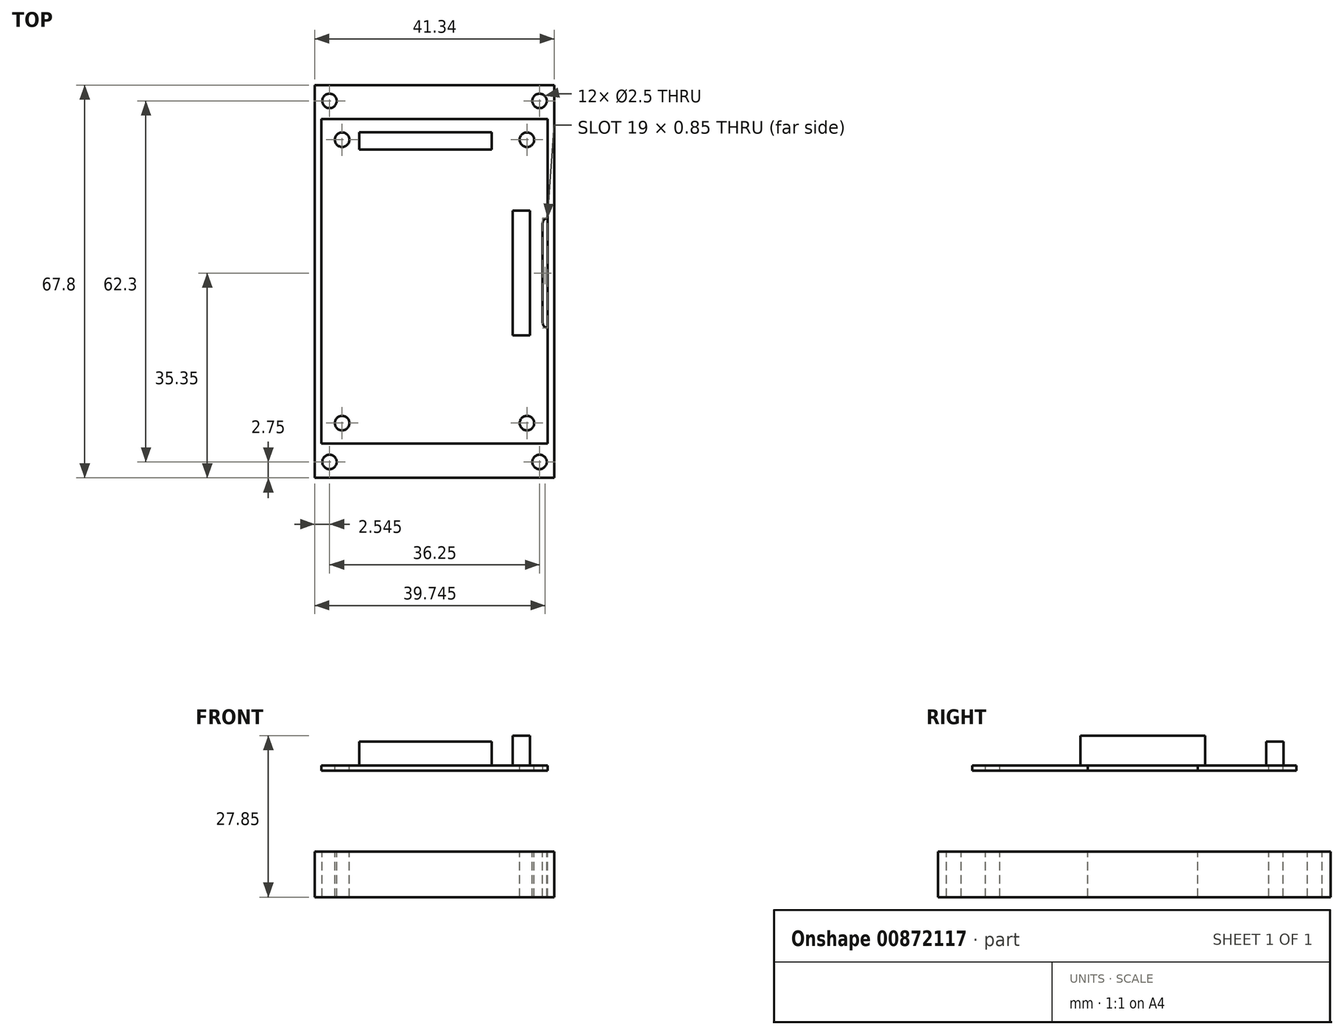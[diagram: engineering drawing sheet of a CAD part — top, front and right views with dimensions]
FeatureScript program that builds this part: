
annotation { "Feature Type Name" : "Feature", "Feature Type Description" : "" }
export const myFeature = defineFeature(function(context is Context, id is Id, definition is map)
    precondition{}
    {
        {
            var Q0;
            Q0=qCreatedBy(makeId("Top.planeOp"),FACE);
            var sketch = newSketch(context, id + "F0", { "sketchPlane" : qUnion([Q0])});
            skLineSegment(sketch, "E0.bottom", {"start": v(-20.67, 33.9) * mm, "end": v(20.68, 33.9) * mm});
            skLineSegment(sketch, "E0.top", {"start": v(-20.68, -33.9) * mm, "end": v(20.67, -33.9) * mm});
            skLineSegment(sketch, "E0.left", {"start": v(-20.67, 33.9) * mm, "end": v(-20.68, -33.9) * mm});
            skLineSegment(sketch, "E0.right", {"start": v(20.68, 33.9) * mm, "end": v(20.67, -33.9) * mm});
            skLineSegment(sketch, "E1", {"start": v(-20.67, 33.9) * mm, "end": v(20.67, -33.9) * mm, "construction": true});
            skSolve(sketch);
        }
        {
            var Q0;
            Q0 = qSketchRegion(id + "F0", true);
            extrude(context, id + "F1", {"entities" : qUnion([Q0]), "depth" : 7.85 * mm, "offsetDistance" : 25 * mm});
        }
        {
            var Q0;
            Q0=makeQuery(id+"F1.opExtrude","CAP_FACE",FACE,{"disambiguationData":[OSD([sQuery(id+"F0.wireOp",EDGE,"E0.bottom"),sQuery(id+"F0.wireOp",EDGE,"E0.top"),sQuery(id+"F0.wireOp",EDGE,"E0.left"),sQuery(id+"F0.wireOp",EDGE,"E0.right")])],"isStart":false});
            var sketch = newSketch(context, id + "F2", { "sketchPlane" : qUnion([Q0])});
            skCircle(sketch, "E2", {"center": v(-18.12, -31.15) * mm, "radius": 1.25 * mm});
            skCircle(sketch, "E3", {"center": v(-18.12, 31.15) * mm, "radius": 1.25 * mm});
            skLineSegment(sketch, "E4", {"start": v(0, 33.9) * mm, "end": v(0, -33.9) * mm, "construction": true});
            skLineSegment(sketch, "E5", {"start": v(-12.64, 29.9) * mm, "end": v(-19.15, 29.9) * mm, "construction": true});
            skLineSegment(sketch, "E6", {"start": v(-13.26, -29.9) * mm, "end": v(-20.68, -29.9) * mm, "construction": true});
            skLineSegment(sketch, "E7", {"start": v(0, 0) * mm, "end": v(-11.7, 0) * mm, "construction": true});
            skLineSegment(sketch, "E8", {"start": v(-19.37, 33.4) * mm, "end": v(-19.37, 27.84) * mm, "construction": true});
            skCircle(sketch, "E9.MirrorC", {"center": v(18.13, 31.15) * mm, "radius": 1.25 * mm});
            skCircle(sketch, "E10.MirrorC", {"center": v(18.12, -31.15) * mm, "radius": 1.25 * mm});
            skSolve(sketch);
        }
        {
            var Q0;
            Q0 = qSketchRegion(id + "F2", true);
            extrude(context, id + "F3", {"entities" : qUnion([Q0]), "operationType" : NewBodyOperationType.REMOVE, "endBound" : BoundingType.THROUGH_ALL, "oppositeDirection" : true, "depth" : 25 * mm, "offsetDistance" : 25 * mm});
        }
        {
            var Q0;
            Q0=makeQuery(id+"F1.opExtrude","CAP_FACE",FACE,{"disambiguationData":[OSD([sQuery(id+"F0.wireOp",EDGE,"E0.bottom"),sQuery(id+"F0.wireOp",EDGE,"E0.top"),sQuery(id+"F0.wireOp",EDGE,"E0.left"),sQuery(id+"F0.wireOp",EDGE,"E0.right")])],"isStart":false});
            cPlane(context, id + "F4", {"entities" : qUnion([Q0]), "cplaneType" : CPlaneType.OFFSET, "offset" : 14 * mm, "width" : 150 * mm, "height" : 150 * mm});
        }
        {
            var Q0;
            Q0=qCreatedBy(id+"F4.planeOp",FACE);
            var sketch = newSketch(context, id + "F5", { "sketchPlane" : qUnion([Q0])});
            skLineSegment(sketch, "E11.bottom", {"start": v(-19.5, 28) * mm, "end": v(19.5, 28) * mm});
            skLineSegment(sketch, "E11.top", {"start": v(-19.5, -28) * mm, "end": v(19.5, -28) * mm});
            skLineSegment(sketch, "E11.left", {"start": v(-19.5, 28) * mm, "end": v(-19.5, -28) * mm});
            skLineSegment(sketch, "E11.right", {"start": v(19.5, 28) * mm, "end": v(19.5, -28) * mm});
            skLineSegment(sketch, "E12", {"start": v(-19.5, 28) * mm, "end": v(19.5, -28) * mm, "construction": true});
            skSolve(sketch);
        }
        {
            var Q0;
            Q0 = qSketchRegion(id + "F5", true);
            extrude(context, id + "F6", {"entities" : qUnion([Q0]), "depth" : .85 * mm, "offsetDistance" : 25 * mm});
        }
        {
            var Q0;
            Q0=makeQuery(id+"F6.opExtrude","CAP_FACE",FACE,{"disambiguationData":[OSD([sQuery(id+"F5.wireOp",EDGE,"E11.bottom"),sQuery(id+"F5.wireOp",EDGE,"E11.top"),sQuery(id+"F5.wireOp",EDGE,"E11.left"),sQuery(id+"F5.wireOp",EDGE,"E11.right")])],"isStart":false});
            var sketch = newSketch(context, id + "F7", { "sketchPlane" : qUnion([Q0])});
            skCircle(sketch, "E13", {"center": v(-15.95, 24.45) * mm, "radius": 1.25 * mm});
            skCircle(sketch, "E14", {"center": v(-15.95, -24.45) * mm, "radius": 1.25 * mm});
            skLineSegment(sketch, "E15", {"start": v(0, 0) * mm, "end": v(-8.76, 0) * mm, "construction": true});
            skLineSegment(sketch, "E16", {"start": v(0, 0) * mm, "end": v(0, 7.08) * mm, "construction": true});
            skLineSegment(sketch, "E17", {"start": v(-18.07, 25.7) * mm, "end": v(-11.88, 25.7) * mm, "construction": true});
            skLineSegment(sketch, "E18", {"start": v(-17.2, 21.13) * mm, "end": v(-17.2, 28.21) * mm, "construction": true});
            skCircle(sketch, "E19.MirrorC", {"center": v(15.95, 24.45) * mm, "radius": 1.25 * mm});
            skCircle(sketch, "E20.MirrorC", {"center": v(15.95, -24.45) * mm, "radius": 1.25 * mm});
            skSolve(sketch);
        }
        {
            var Q0;
            Q0 = qSketchRegion(id + "F7", true);
            extrude(context, id + "F8", {"entities" : qUnion([Q0]), "operationType" : NewBodyOperationType.REMOVE, "endBound" : BoundingType.THROUGH_ALL, "oppositeDirection" : true, "depth" : 25 * mm, "offsetDistance" : 25 * mm});
        }
        {
            var Q0;
            Q0=makeQuery(id+"F6.opExtrude","CAP_FACE",FACE,{"disambiguationData":[OSD([sQuery(id+"F5.wireOp",EDGE,"E11.bottom"),sQuery(id+"F5.wireOp",EDGE,"E11.top"),sQuery(id+"F5.wireOp",EDGE,"E11.left"),sQuery(id+"F5.wireOp",EDGE,"E11.right")])],"isStart":false});
            var sketch = newSketch(context, id + "F9", { "sketchPlane" : qUnion([Q0])});
            skLineSegment(sketch, "E21.bottom", {"start": v(13.5, 12.2) * mm, "end": v(16.5, 12.2) * mm});
            skLineSegment(sketch, "E21.top", {"start": v(13.5, -9.3) * mm, "end": v(16.5, -9.3) * mm});
            skLineSegment(sketch, "E21.left", {"start": v(13.5, 12.2) * mm, "end": v(13.5, -9.3) * mm});
            skLineSegment(sketch, "E21.right", {"start": v(16.5, 12.2) * mm, "end": v(16.5, -9.3) * mm});
            skLineSegment(sketch, "E22.bottom", {"start": v(-13, 25.75) * mm, "end": v(-1.5, 25.75) * mm});
            skLineSegment(sketch, "E22.top", {"start": v(-13, 22.75) * mm, "end": v(-1.5, 22.75) * mm});
            skLineSegment(sketch, "E22.left", {"start": v(-13, 25.75) * mm, "end": v(-13, 22.75) * mm});
            skLineSegment(sketch, "E23.bottom", {"start": v(-1.6, 25.75) * mm, "end": v(9.9, 25.75) * mm});
            skLineSegment(sketch, "E23.top", {"start": v(-1.6, 22.75) * mm, "end": v(9.9, 22.75) * mm});
            skLineSegment(sketch, "E23.left", {"start": v(-1.6, 25.75) * mm, "end": v(-1.6, 22.75) * mm});
            skLineSegment(sketch, "E23.right", {"start": v(9.9, 25.75) * mm, "end": v(9.9, 22.75) * mm});
            skLineSegment(sketch, "E24", {"start": v(-1.5, 25.75) * mm, "end": v(-1.5, 22.75) * mm});
            skSolve(sketch);
        }
        {
            var Q0;
            Q0=makeQuery(id+"F9.imprint","IMPRINT",FACE,{"disambiguationData":[TD([[makeQuery(id+"F9.imprint","IMPRINT",EDGE,{"derivedFrom":sQuery(id+"F9.wireOp",EDGE,"E21.bottom")}),-1.0]])]});
            extrude(context, id + "F10", {"entities" : qUnion([Q0]), "depth" : (6 - .85) * mm, "offsetDistance" : 25 * mm});
        }
        {
            var Q0;
            Q0=makeQuery(id+"F9.imprint","IMPRINT",FACE,{"disambiguationData":[TD([[makeQuery(id+"F9.imprint","IMPRINT",EDGE,{"derivedFrom":sQuery(id+"F9.wireOp",EDGE,"E22.bottom")}),-1.0]])]});
            var Q1;
            {var subQ0=sQuery(id+"F9.wireOp",EDGE,"E23.right");Q1=makeQuery(id+"F9.imprint","IMPRINT",FACE,{"disambiguationData":[TD([[makeQuery(id+"F9.imprint","IMPRINT",EDGE,{"derivedFrom":subQ0}),-1.0]])]});}
            extrude(context, id + "F11", {"entities" : qUnion([Q0, Q1]), "depth" : (5 - .85) * mm, "offsetDistance" : 25 * mm});
        }
        {
            var Q0;
            Q0=makeQuery(id+"F6.opExtrude","CAP_FACE",FACE,{"disambiguationData":[OSD([sQuery(id+"F5.wireOp",EDGE,"E11.bottom"),sQuery(id+"F5.wireOp",EDGE,"E11.top"),sQuery(id+"F5.wireOp",EDGE,"E11.left"),sQuery(id+"F5.wireOp",EDGE,"E11.right")])],"isStart":false});
            var sketch = newSketch(context, id + "F12", { "sketchPlane" : qUnion([Q0])});
            skLineSegment(sketch, "E25.bottom", {"start": v(19.5, 10.95) * mm, "end": v(18.65, 10.95) * mm});
            skLineSegment(sketch, "E25.top", {"start": v(19.5, -8.05) * mm, "end": v(18.65, -8.05) * mm});
            skLineSegment(sketch, "E25.left", {"start": v(19.5, 10.95) * mm, "end": v(19.5, -8.05) * mm});
            skLineSegment(sketch, "E25.right", {"start": v(18.65, 10.95) * mm, "end": v(18.65, -8.05) * mm});
            skLineSegment(sketch, "E26", {"start": v(18.65, 1.45) * mm, "end": v(16.5, 1.45) * mm, "construction": true});
            skSolve(sketch);
        }
        {
            var Q0;
            Q0 = qSketchRegion(id + "F12", true);
            extrude(context, id + "F13", {"entities" : qUnion([Q0]), "operationType" : NewBodyOperationType.REMOVE, "endBound" : BoundingType.THROUGH_ALL, "oppositeDirection" : true, "depth" : 25 * mm, "offsetDistance" : 25 * mm});
        }
        {
            var Q0;
            Q0=makeQuery(id+"F13.boolean.opBoolean","COPY",EDGE,{"derivedFrom":makeQuery(id+"F13.opExtrude","SWEPT_EDGE",EDGE,{"disambiguationData":[OSD([sQuery(id+"F12.wireOp",EDGE,"E25.bottom"),sQuery(id+"F12.wireOp",EDGE,"E25.right")])]})});
            var Q1;
            Q1=makeQuery(id+"F13.boolean.opBoolean","COPY",EDGE,{"derivedFrom":makeQuery(id+"F13.opExtrude","SWEPT_EDGE",EDGE,{"disambiguationData":[OSD([sQuery(id+"F12.wireOp",EDGE,"E25.top"),sQuery(id+"F12.wireOp",EDGE,"E25.right")])]})});
            fillet(context, id + "F14", {"entities" : qUnion([Q0, Q1]), "radius" : 1 * mm, "tangentPropagation" : true, "allowEdgeOverflow" : false});
        }
    });
